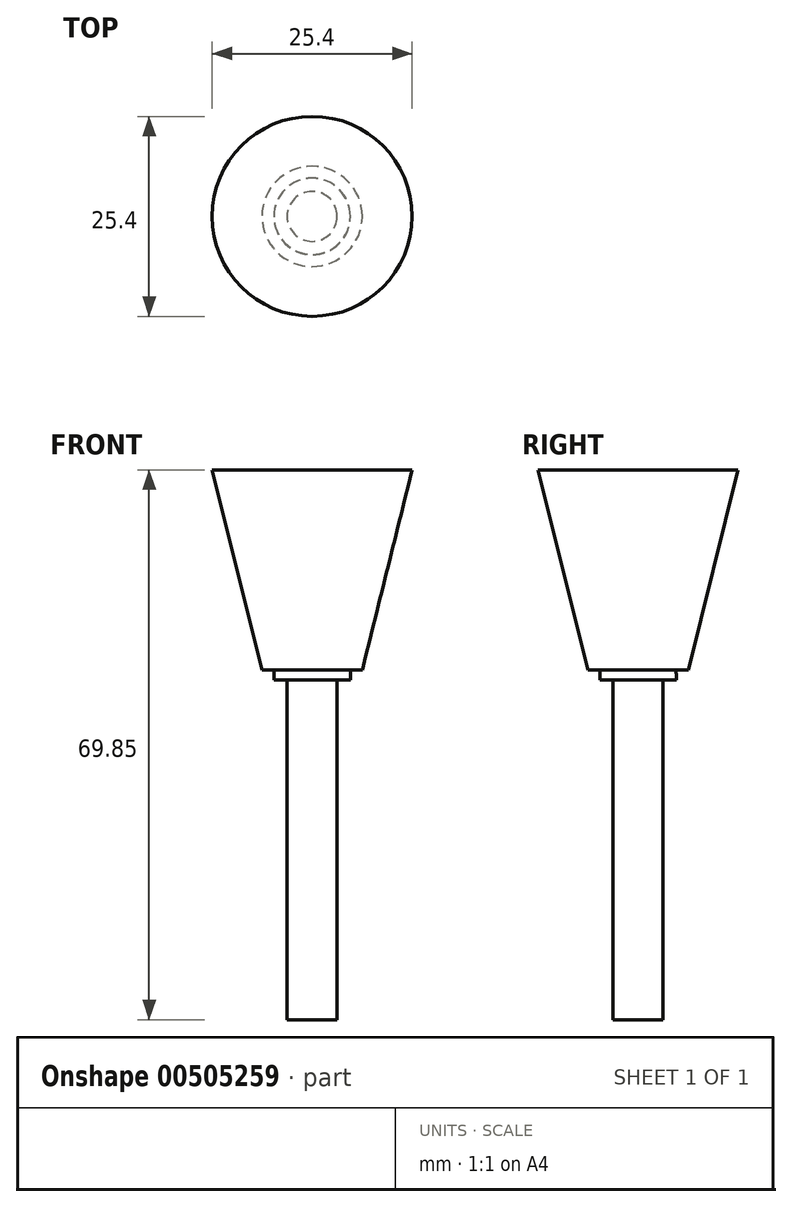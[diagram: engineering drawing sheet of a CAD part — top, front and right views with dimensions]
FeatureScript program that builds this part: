
annotation { "Feature Type Name" : "Feature", "Feature Type Description" : "" }
export const myFeature = defineFeature(function(context is Context, id is Id, definition is map)
    precondition{}
    {
        {
            var Q0;
            Q0=qCreatedBy(makeId("Right.planeOp"),FACE);
            var sketch = newSketch(context, id + "F0", { "sketchPlane" : qUnion([Q0])});
            skLineSegment(sketch, "E0", {"start": v(-12.7, 25.4) * mm, "end": v(-6.37, 0) * mm});
            skLineSegment(sketch, "E1", {"start": v(-12.7, 25.4) * mm, "end": v(0, 25.4) * mm});
            skLineSegment(sketch, "E2", {"start": v(-6.35, -10.6) * mm, "end": v(-6.35, -44.45) * mm});
            skLineSegment(sketch, "E3", {"start": v(-6.37, 0) * mm, "end": v(-4.84, 0) * mm});
            skArc(sketch, "E4", {"start": v(-6.35, -10.6) * mm, "mid": v(-5.22, -5.36) * mm, "end": v(-4.84, 0) * mm});
            skLineSegment(sketch, "E5", {"start": v(-6.35, -44.45) * mm, "end": v(0, -44.45) * mm});
            skLineSegment(sketch, "E6", {"start": v(0, 25.4) * mm, "end": v(0, -44.45) * mm});
            skSolve(sketch);
        }
        {
            var Q0;
            Q0=makeQuery(id+"F0.imprint","IMPRINT",FACE,{"disambiguationData":[TD([[makeQuery(id+"F0.imprint","IMPRINT",EDGE,{"derivedFrom":sQuery(id+"F0.wireOp",EDGE,"E0")}),1.0]])]});
            var Q1;
            Q1=sQuery(id+"F0.wireOp",EDGE,"E6");
            revolve(context, id + "F1", {"entities" : qUnion([Q0]), "axis" : qUnion([Q1]), "revolveType" : RevolveType.FULL});
        }
        {
            var Q0;
            Q0=qCreatedBy(makeId("Right.planeOp"),FACE);
            var sketch = newSketch(context, id + "F2", { "sketchPlane" : qUnion([Q0])});
            skLineSegment(sketch, "E7.bottom", {"start": v(-3.18, -1.27) * mm, "end": v(-14.12, -1.27) * mm});
            skLineSegment(sketch, "E7.top", {"start": v(-3.17, -44.45) * mm, "end": v(-14.12, -44.45) * mm});
            skLineSegment(sketch, "E7.left", {"start": v(-3.18, -1.27) * mm, "end": v(-3.17, -44.45) * mm});
            skLineSegment(sketch, "E7.right", {"start": v(-14.12, -1.27) * mm, "end": v(-14.12, -44.45) * mm});
            skSolve(sketch);
        }
        {
            var Q0;
            Q0=makeQuery(id+"F2.imprint","IMPRINT",FACE,{"disambiguationData":[TD([[makeQuery(id+"F2.imprint","IMPRINT",EDGE,{"derivedFrom":sQuery(id+"F2.wireOp",EDGE,"E7.bottom")}),1.0]])]});
            var Q1;
            Q1=sQuery(id+"F0.wireOp",EDGE,"E6");
            revolve(context, id + "F3", {"operationType" : NewBodyOperationType.REMOVE, "entities" : qUnion([Q0]), "axis" : qUnion([Q1]), "revolveType" : RevolveType.FULL, "oppositeDirection" : true});
        }
    });
